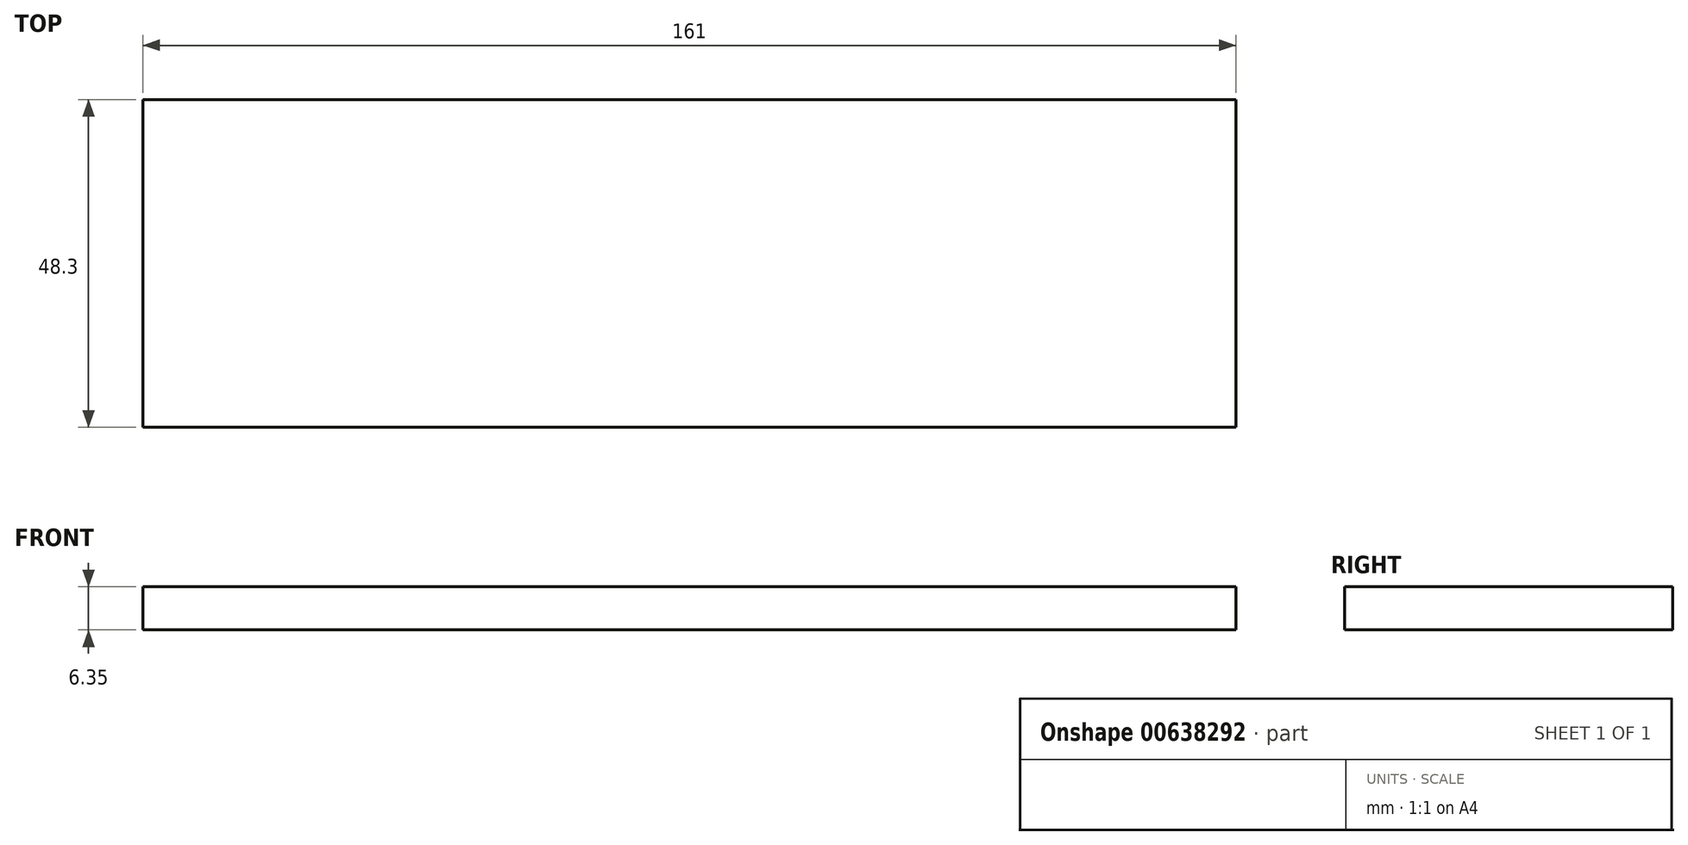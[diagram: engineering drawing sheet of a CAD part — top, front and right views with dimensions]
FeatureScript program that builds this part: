
annotation { "Feature Type Name" : "Feature", "Feature Type Description" : "" }
export const myFeature = defineFeature(function(context is Context, id is Id, definition is map)
    precondition{}
    {
        {
            var Q0;
            Q0=qCreatedBy(makeId("Top.planeOp"),FACE);
            var sketch = newSketch(context, id + "F0", { "sketchPlane" : qUnion([Q0])});
            skLineSegment(sketch, "E0.bottom", {"start": v(0, 0) * mm, "end": v(161, 0) * mm});
            skLineSegment(sketch, "E0.top", {"start": v(0, -48.3) * mm, "end": v(161, -48.3) * mm});
            skLineSegment(sketch, "E0.left", {"start": v(0, 0) * mm, "end": v(0, -48.3) * mm});
            skLineSegment(sketch, "E0.right", {"start": v(161, 0) * mm, "end": v(161, -48.3) * mm});
            skSolve(sketch);
        }
        {
            var Q0;
            Q0=makeQuery(id+"F0.imprint","IMPRINT",FACE,{"disambiguationData":[TD([[makeQuery(id+"F0.imprint","IMPRINT",EDGE,{"derivedFrom":sQuery(id+"F0.wireOp",EDGE,"E0.bottom")}),-1.0]])]});
            extrude(context, id + "F1", {"entities" : qUnion([Q0]), "depth" : 6.35 * mm, "offsetDistance" : 25.4 * mm});
        }
    });
